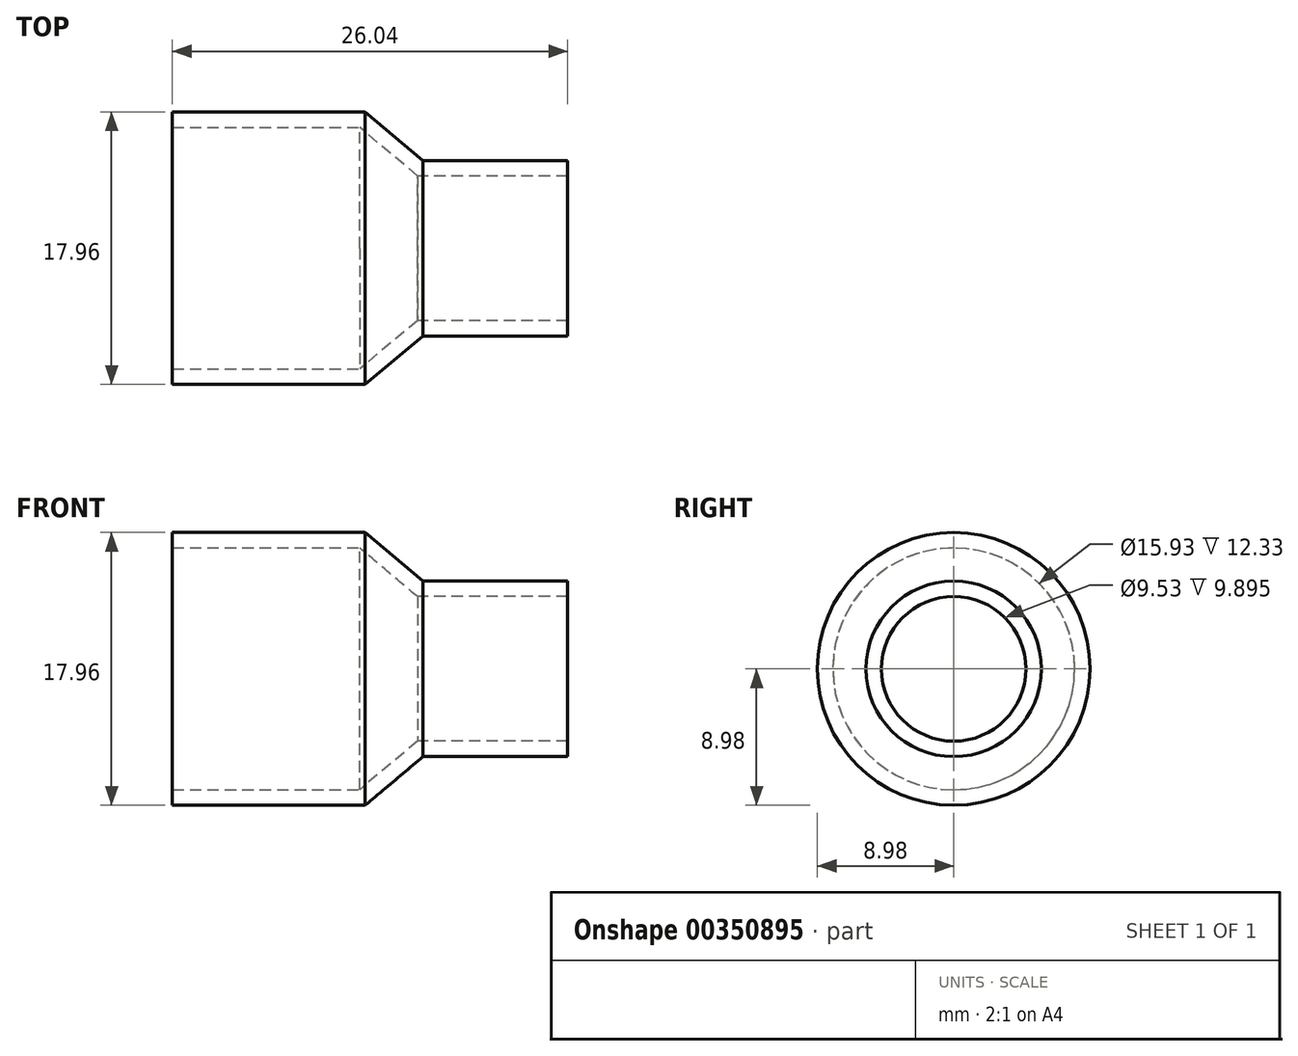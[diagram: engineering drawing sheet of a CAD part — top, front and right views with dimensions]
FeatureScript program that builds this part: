
annotation { "Feature Type Name" : "Feature", "Feature Type Description" : "" }
export const myFeature = defineFeature(function(context is Context, id is Id, definition is map)
    precondition{}
    {
        {
            var Q0;
            Q0=qCreatedBy(makeId("Right.planeOp"),FACE);
            var sketch = newSketch(context, id + "F0", { "sketchPlane" : qUnion([Q0])});
            skCircle(sketch, "E0", {"center": v(0, 0) * mm, "radius": 8.98 * mm});
            skSolve(sketch);
        }
        {
            var Q0;
            Q0=qSketchRegion(id+"F0",true);
            extrude(context, id + "F1", {"entities" : qUnion([Q0]), "oppositeDirection" : true, "depth" : 12.7 * mm});
        }
        {
            var Q0;
            Q0=qCreatedBy(makeId("Right.planeOp"),FACE);
            cPlane(context, id + "F2", {"entities" : qUnion([Q0]), "cplaneType" : CPlaneType.OFFSET, "offset" : 3.8 * mm, "width" : 152.4 * mm, "height" : 152.4 * mm});
        }
        {
            var Q0;
            Q0=qCreatedBy(id+"F2.planeOp",FACE);
            var sketch = newSketch(context, id + "F3", { "sketchPlane" : qUnion([Q0])});
            skPoint(sketch, "E1.0", {"position": v(0, 0) * mm});
            skCircle(sketch, "E2", {"center": v(0, 0) * mm, "radius": 5.78 * mm});
            skSolve(sketch);
        }
        {
            var Q0;
            Q0=qSketchRegion(id+"F3",true);
            extrude(context, id + "F4", {"entities" : qUnion([Q0]), "depth" : 9.52 * mm});
        }
        {
            var Q0;
            Q0=makeQuery(id+"F1.opExtrude","CAP_FACE",FACE,{"disambiguationData":[OSD([sQuery(id+"F0.wireOp",EDGE,"FSnA3JPl-jaDT-1N9C-D5yt-aIQ6gAFVFGIr"),sQuery(id+"F0.wireOp",EDGE,"E0")])],"isStart":true});
            var Q1;
            Q1=makeQuery(id+"F4.opExtrude","CAP_FACE",FACE,{"disambiguationData":[OSD([sQuery(id+"F3.wireOp",EDGE,"bssw4aSf-YQa8-k349-BioW-mXQyCm2wpGI0"),sQuery(id+"F3.wireOp",EDGE,"E2")])],"isStart":true});
            loft(context, id + "F5", {"operationType" : NewBodyOperationType.ADD, "sheetProfilesArray" : [{ "sheetProfileEntities" : qUnion([Q0]) }, { "sheetProfileEntities" : qUnion([Q1]) }]});
        }
        {
            var Q0;
            Q0=makeQuery(id+"F4.opExtrude","CAP_FACE",FACE,{"disambiguationData":[OSD([sQuery(id+"F3.wireOp",EDGE,"E2")])],"isStart":false});
            var Q1;
            Q1=makeQuery(id+"F1.opExtrude","CAP_FACE",FACE,{"disambiguationData":[OSD([sQuery(id+"F0.wireOp",EDGE,"E0")])],"isStart":false});
            shell(context, id + "F6", {"entities" : qUnion([Q0, Q1]), "thickness" : 1.02 * mm});
        }
    });
